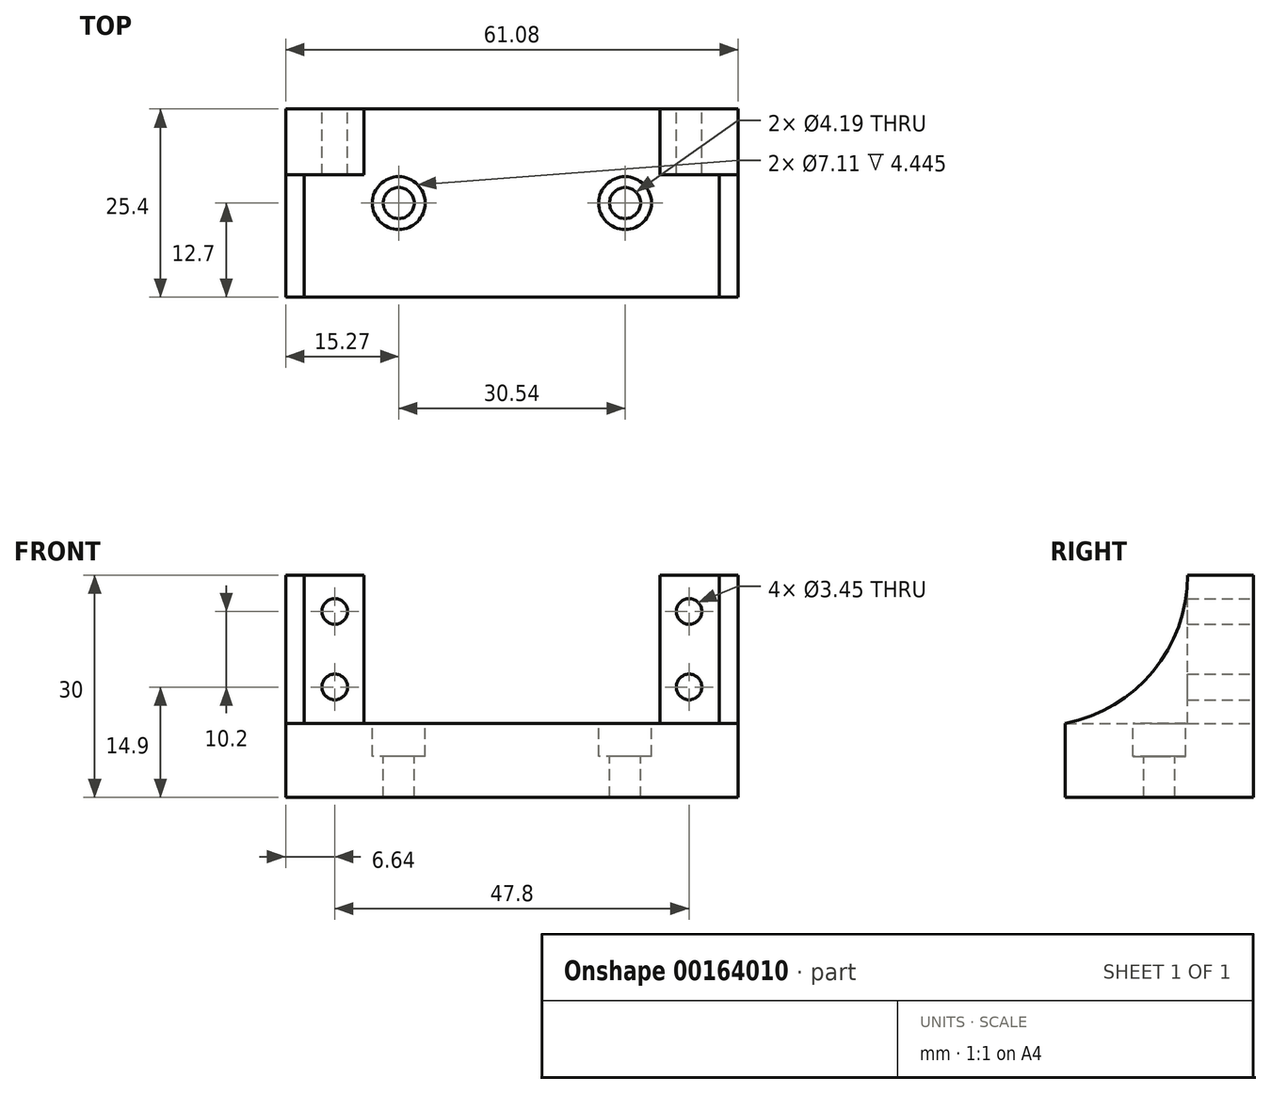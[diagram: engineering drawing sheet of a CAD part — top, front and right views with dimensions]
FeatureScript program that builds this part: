
annotation { "Feature Type Name" : "Feature", "Feature Type Description" : "" }
export const myFeature = defineFeature(function(context is Context, id is Id, definition is map)
    precondition{}
    {
        {
            var Q0;
            Q0=qCreatedBy(makeId("Front.planeOp"),FACE);
            var sketch = newSketch(context, id + "F0", { "sketchPlane" : qUnion([Q0])});
            skLineSegment(sketch, "E0.bottom", {"start": v(0, 0) * mm, "end": v(56, 0) * mm});
            skLineSegment(sketch, "E0.top", {"start": v(0, 30) * mm, "end": v(8, 30) * mm});
            skLineSegment(sketch, "E0.left", {"start": v(0, 0) * mm, "end": v(0, 30) * mm});
            skLineSegment(sketch, "E0.right", {"start": v(56, 0) * mm, "end": v(56, 30) * mm});
            skLineSegment(sketch, "E1.top", {"start": v(8, 10) * mm, "end": v(48, 10) * mm});
            skLineSegment(sketch, "E1.left", {"start": v(8, 30) * mm, "end": v(8, 10) * mm});
            skLineSegment(sketch, "E1.right", {"start": v(48, 30) * mm, "end": v(48, 10) * mm});
            skCircle(sketch, "E2", {"center": v(4.1, 25.1) * mm, "radius": 1.73 * mm});
            skCircle(sketch, "E3", {"center": v(4.1, 14.9) * mm, "radius": 1.73 * mm});
            skCircle(sketch, "E4", {"center": v(51.9, 25.1) * mm, "radius": 1.73 * mm});
            skCircle(sketch, "E5", {"center": v(51.9, 14.9) * mm, "radius": 1.73 * mm});
            skLineSegment(sketch, "E6", {"start": v(28, 30) * mm, "end": v(28, 10) * mm, "construction": true});
            skLineSegment(sketch, "E7", {"start": v(8, 20) * mm, "end": v(48, 20) * mm, "construction": true});
            skLineSegment(sketch, "E8.trimOffspring", {"start": v(48, 30) * mm, "end": v(56, 30) * mm});
            skSolve(sketch);
        }
        {
            var Q0;
            Q0 = qSketchRegion(id + "F0", true);
            extrude(context, id + "F1", {"entities" : qUnion([Q0]), "depth" : 8.9 * mm});
        }
        {
            var Q0;
            Q0=makeQuery(id+"F1.opExtrude","CAP_FACE",FACE,{"disambiguationData":[OSD([sQuery(id+"F0.wireOp",EDGE,"E0.bottom"),sQuery(id+"F0.wireOp",EDGE,"E0.top"),sQuery(id+"F0.wireOp",EDGE,"E0.left"),sQuery(id+"F0.wireOp",EDGE,"E0.right"),sQuery(id+"F0.wireOp",EDGE,"E1.top"),sQuery(id+"F0.wireOp",EDGE,"E1.left"),sQuery(id+"F0.wireOp",EDGE,"E1.right"),sQuery(id+"F0.wireOp",EDGE,"E2"),sQuery(id+"F0.wireOp",EDGE,"E3"),sQuery(id+"F0.wireOp",EDGE,"E4"),sQuery(id+"F0.wireOp",EDGE,"E5"),sQuery(id+"F0.wireOp",EDGE,"E8.trimOffspring")])],"isStart":false});
            var sketch = newSketch(context, id + "F2", { "sketchPlane" : qUnion([Q0])});
            skLineSegment(sketch, "E9.bottom", {"start": v(0, 0) * mm, "end": v(56, 0) * mm});
            skLineSegment(sketch, "E9.top", {"start": v(0, 10) * mm, "end": v(56, 10) * mm});
            skLineSegment(sketch, "E9.left", {"start": v(0, 0) * mm, "end": v(0, 10) * mm});
            skLineSegment(sketch, "E9.right", {"start": v(56, 0) * mm, "end": v(56, 10) * mm});
            skSolve(sketch);
        }
        {
            var Q0;
            Q0 = qSketchRegion(id + "F2", true);
            extrude(context, id + "F3", {"entities" : qUnion([Q0]), "operationType" : NewBodyOperationType.ADD, "depth" : 16.5 * mm});
        }
        {
            var Q0;
            Q0=makeQuery(id+"F3.boolean.opBoolean","MERGE",FACE,{"derivedFrom":[makeQuery(id+"F1.opExtrude","SWEPT_FACE",FACE,{"disambiguationData":[OSD([sQuery(id+"F0.wireOp",EDGE,"E0.right")])]}),makeQuery(id+"F3.opExtrude","SWEPT_FACE",FACE,{"disambiguationData":[OSD([sQuery(id+"F2.wireOp",EDGE,"E9.right")])]})]});
            var sketch = newSketch(context, id + "F4", { "sketchPlane" : qUnion([Q0])});
            skLineSegment(sketch, "E10", {"start": v(-8.89, 30) * mm, "end": v(0, 30) * mm});
            skLineSegment(sketch, "E11", {"start": v(0, 30) * mm, "end": v(0, 0) * mm});
            skLineSegment(sketch, "E12", {"start": v(0, 0) * mm, "end": v(-25.4, 0) * mm});
            skLineSegment(sketch, "E13", {"start": v(-25.4, 0) * mm, "end": v(-25.4, 10) * mm});
            skArc(sketch, "E14", {"start": v(-25.4, 10) * mm, "mid": v(-13.55, 17.03) * mm, "end": v(-8.89, 30) * mm});
            skSolve(sketch);
        }
        {
            var Q0;
            Q0 = qSketchRegion(id + "F4", true);
            extrude(context, id + "F5", {"entities" : qUnion([Q0]), "operationType" : NewBodyOperationType.ADD, "depth" : 2.54 * mm});
        }
        {
            var Q0;
            Q0=makeQuery(id+"F3.boolean.opBoolean","MERGE",FACE,{"derivedFrom":[makeQuery(id+"F1.opExtrude","SWEPT_FACE",FACE,{"disambiguationData":[OSD([sQuery(id+"F0.wireOp",EDGE,"E0.left")])]}),makeQuery(id+"F3.opExtrude","SWEPT_FACE",FACE,{"disambiguationData":[OSD([sQuery(id+"F2.wireOp",EDGE,"E9.left")])]})]});
            var sketch = newSketch(context, id + "F6", { "sketchPlane" : qUnion([Q0])});
            skLineSegment(sketch, "E15", {"start": v(8.9, 30) * mm, "end": v(0, 30) * mm});
            skLineSegment(sketch, "E16", {"start": v(0, 30) * mm, "end": v(0, 0) * mm});
            skLineSegment(sketch, "E17", {"start": v(0, 0) * mm, "end": v(25.4, 0) * mm});
            skLineSegment(sketch, "E18", {"start": v(25.4, 0) * mm, "end": v(25.4, 10) * mm});
            skArc(sketch, "E19", {"start": v(8.9, 30) * mm, "mid": v(13.55, 17.03) * mm, "end": v(25.4, 10) * mm});
            skSolve(sketch);
        }
        {
            var Q0;
            Q0=makeQuery(id+"F6.imprint","IMPRINT",FACE,{"disambiguationData":[TD([[makeQuery(id+"F6.imprint","IMPRINT",EDGE,{"derivedFrom":sQuery(id+"F6.wireOp",EDGE,"E15")}),1.0]])]});
            var Q1;
            Q1=makeQuery(id+"F6.imprint","IMPRINT",FACE,{"disambiguationData":[TD([[makeQuery(id+"F6.imprint","IMPRINT",EDGE,{"derivedFrom":sQuery(id+"F6.wireOp",EDGE,"E19")}),-1.0]])]});
            extrude(context, id + "F7", {"entities" : qUnion([Q0, Q1]), "operationType" : NewBodyOperationType.ADD, "depth" : 2.54 * mm});
        }
        {
            var Q0;
            Q0=makeQuery(id+"F3.boolean.opBoolean","MERGE",FACE,{"derivedFrom":[makeQuery(id+"F1.opExtrude","SWEPT_FACE",FACE,{"disambiguationData":[OSD([sQuery(id+"F0.wireOp",EDGE,"E1.top")])]}),makeQuery(id+"F3.opExtrude","SWEPT_FACE",FACE,{"disambiguationData":[OSD([sQuery(id+"F2.wireOp",EDGE,"E9.top")])]})]});
            var sketch = newSketch(context, id + "F8", { "sketchPlane" : qUnion([Q0])});
            skLineSegment(sketch, "E20", {"start": v(28, 0) * mm, "end": v(28, -25.4) * mm, "construction": true});
            skLineSegment(sketch, "E21", {"start": v(0, -12.7) * mm, "end": v(56, -12.7) * mm, "construction": true});
            skCircle(sketch, "E22", {"center": v(12.73, -12.7) * mm, "radius": 2.1 * mm});
            skCircle(sketch, "E23", {"center": v(43.27, -12.7) * mm, "radius": 2.1 * mm});
            skSolve(sketch);
        }
        {
            var Q0;
            Q0 = qSketchRegion(id + "F8", true);
            extrude(context, id + "F9", {"entities" : qUnion([Q0]), "operationType" : NewBodyOperationType.REMOVE, "endBound" : BoundingType.THROUGH_ALL, "oppositeDirection" : true, "depth" : 25.4 * mm});
        }
        {
            var Q0;
            Q0=makeQuery(id+"F3.boolean.opBoolean","MERGE",FACE,{"derivedFrom":[makeQuery(id+"F1.opExtrude","SWEPT_FACE",FACE,{"disambiguationData":[OSD([sQuery(id+"F0.wireOp",EDGE,"E1.top")])]}),makeQuery(id+"F3.opExtrude","SWEPT_FACE",FACE,{"disambiguationData":[OSD([sQuery(id+"F2.wireOp",EDGE,"E9.top")])]})]});
            var sketch = newSketch(context, id + "F10", { "sketchPlane" : qUnion([Q0])});
            skCircle(sketch, "E24", {"center": v(12.73, -12.7) * mm, "radius": 3.56 * mm});
            skCircle(sketch, "E25", {"center": v(43.27, -12.7) * mm, "radius": 3.56 * mm});
            skSolve(sketch);
        }
        {
            var Q0;
            Q0 = qSketchRegion(id + "F10", true);
            extrude(context, id + "F11", {"entities" : qUnion([Q0]), "operationType" : NewBodyOperationType.REMOVE, "oppositeDirection" : true, "depth" : 4.44 * mm});
        }
    });
